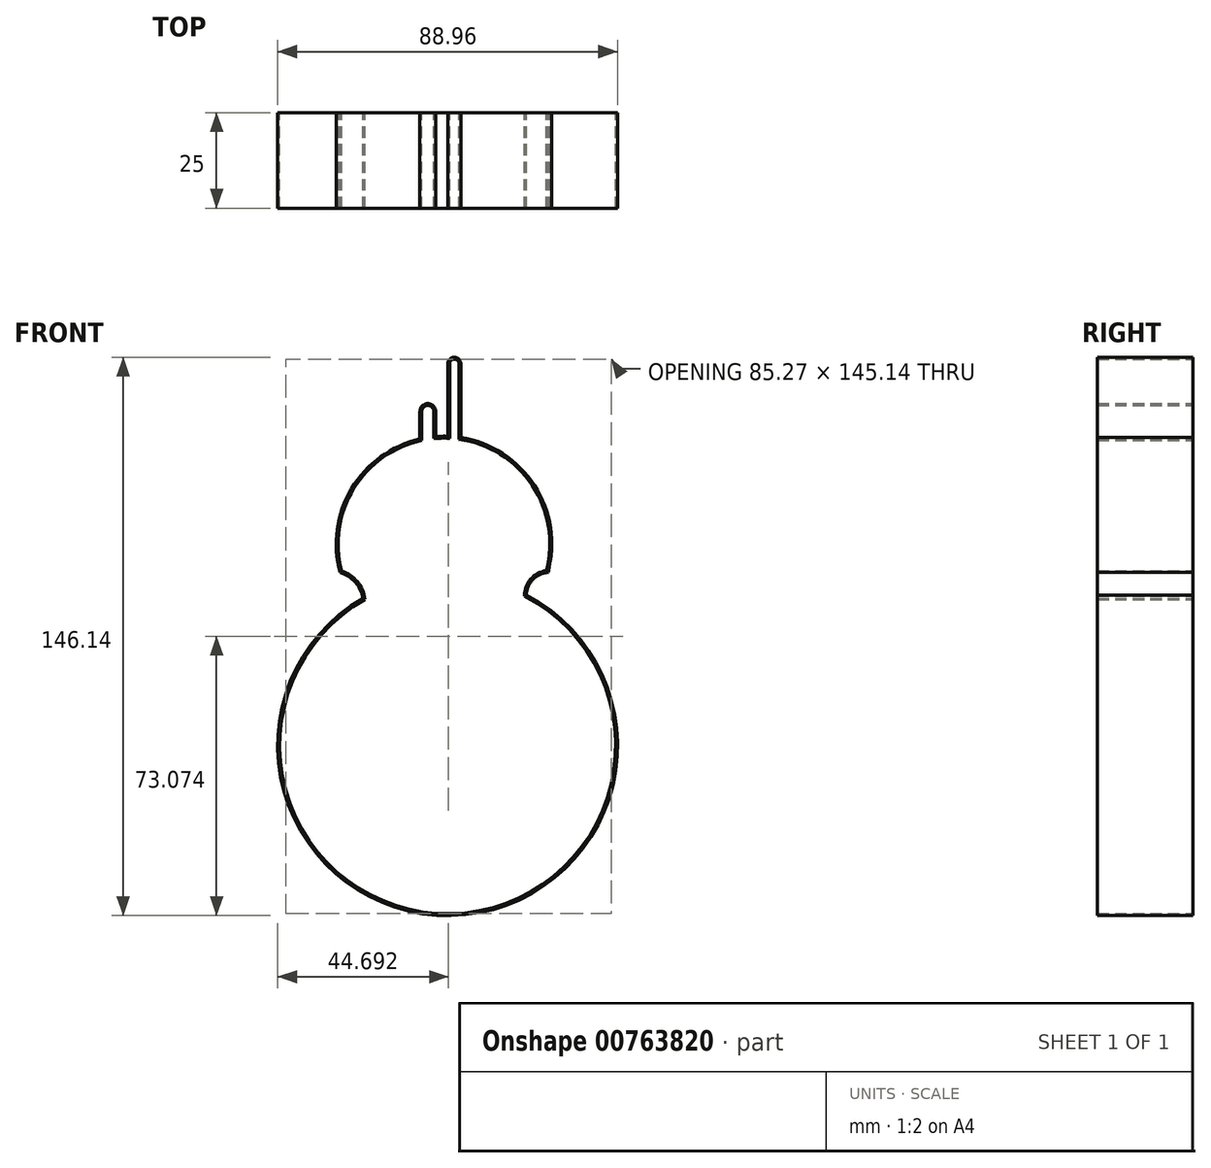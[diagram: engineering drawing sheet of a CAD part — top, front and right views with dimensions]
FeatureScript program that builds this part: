
annotation { "Feature Type Name" : "Feature", "Feature Type Description" : "" }
export const myFeature = defineFeature(function(context is Context, id is Id, definition is map)
    precondition{}
    {
        {
            var Q0;
            Q0=qCreatedBy(makeId("Front.planeOp"),FACE);
            var sketch = newSketch(context, id + "F0", { "sketchPlane" : qUnion([Q0])});
            skArc(sketch, "E0", {"start": v(-22.18, 38.56) * mm, "mid": v(0.9, -44.47) * mm, "end": v(20.61, 39.42) * mm});
            skArc(sketch, "E1", {"start": v(26.27, 45.32) * mm, "mid": v(22.74, 68.08) * mm, "end": v(3.43, 80.63) * mm});
            skArc(sketch, "E2", {"start": v(-22.18, 38.56) * mm, "mid": v(-24.21, 42.8) * mm, "end": v(-28.2, 45.31) * mm});
            skArc(sketch, "E3", {"start": v(26.27, 45.32) * mm, "mid": v(22.28, 43.49) * mm, "end": v(20.61, 39.42) * mm});
            skLineSegment(sketch, "E4", {"start": v(-7.26, 80.27) * mm, "end": v(-7.26, 87.45) * mm});
            skLineSegment(sketch, "E5", {"start": v(-3.12, 87.45) * mm, "end": v(-3.12, 80.9) * mm});
            skLineSegment(sketch, "E6", {"start": v(0, 80.96) * mm, "end": v(0, 99.95) * mm});
            skLineSegment(sketch, "E7", {"start": v(3.43, 99.95) * mm, "end": v(3.43, 80.63) * mm});
            skArc(sketch, "E8.trimOffspring", {"start": v(0, 80.96) * mm, "mid": v(-1.56, 80.97) * mm, "end": v(-3.12, 80.9) * mm});
            skArc(sketch, "E9.trimOffspring", {"start": v(-7.26, 80.27) * mm, "mid": v(-25.18, 67.25) * mm, "end": v(-28.2, 45.31) * mm});
            skArc(sketch, "E10", {"start": v(-3.12, 87.45) * mm, "mid": v(-5.19, 89.52) * mm, "end": v(-7.26, 87.45) * mm});
            skArc(sketch, "E11", {"start": v(3.43, 99.95) * mm, "mid": v(1.72, 101.66) * mm, "end": v(0, 99.95) * mm});
            skArc(sketch, "E12.0", {"start": v(-6.76, 79.86) * mm, "mid": v(-24.57, 67.28) * mm, "end": v(-27.78, 45.71) * mm});
            skLineSegment(sketch, "E13.0", {"start": v(-3.62, 87.45) * mm, "end": v(-3.62, 80.35) * mm});
            skArc(sketch, "E14.0", {"start": v(-3.62, 87.45) * mm, "mid": v(-5.19, 89.02) * mm, "end": v(-6.76, 87.45) * mm});
            skLineSegment(sketch, "E15.0", {"start": v(-6.76, 79.86) * mm, "end": v(-6.76, 87.45) * mm});
            skArc(sketch, "E16.0", {"start": v(0.5, 80.44) * mm, "mid": v(-1.56, 80.47) * mm, "end": v(-3.62, 80.35) * mm});
            skLineSegment(sketch, "E17.0", {"start": v(0.5, 80.44) * mm, "end": v(0.5, 99.95) * mm});
            skArc(sketch, "E18.0", {"start": v(2.93, 99.95) * mm, "mid": v(1.72, 101.16) * mm, "end": v(0.5, 99.95) * mm});
            skLineSegment(sketch, "E19.0", {"start": v(2.93, 99.95) * mm, "end": v(2.93, 80.2) * mm});
            skArc(sketch, "E20.0", {"start": v(25.88, 45.79) * mm, "mid": v(22.11, 68.13) * mm, "end": v(2.93, 80.2) * mm});
            skArc(sketch, "E21.0", {"start": v(25.88, 45.79) * mm, "mid": v(21.7, 43.58) * mm, "end": v(20.11, 39.11) * mm});
            skArc(sketch, "E22.0", {"start": v(-21.64, 38.3) * mm, "mid": v(0.87, -43.97) * mm, "end": v(20.11, 39.11) * mm});
            skArc(sketch, "E23.0", {"start": v(-21.64, 38.3) * mm, "mid": v(-23.63, 42.9) * mm, "end": v(-27.78, 45.71) * mm});
            skSolve(sketch);
        }
        {
            var Q0;
            Q0 = qSketchRegion(id + "F0", true);
            extrude(context, id + "F1", {"entities" : qUnion([Q0]), "depth" : 25 * mm, "offsetDistance" : 25 * mm});
        }
    });
